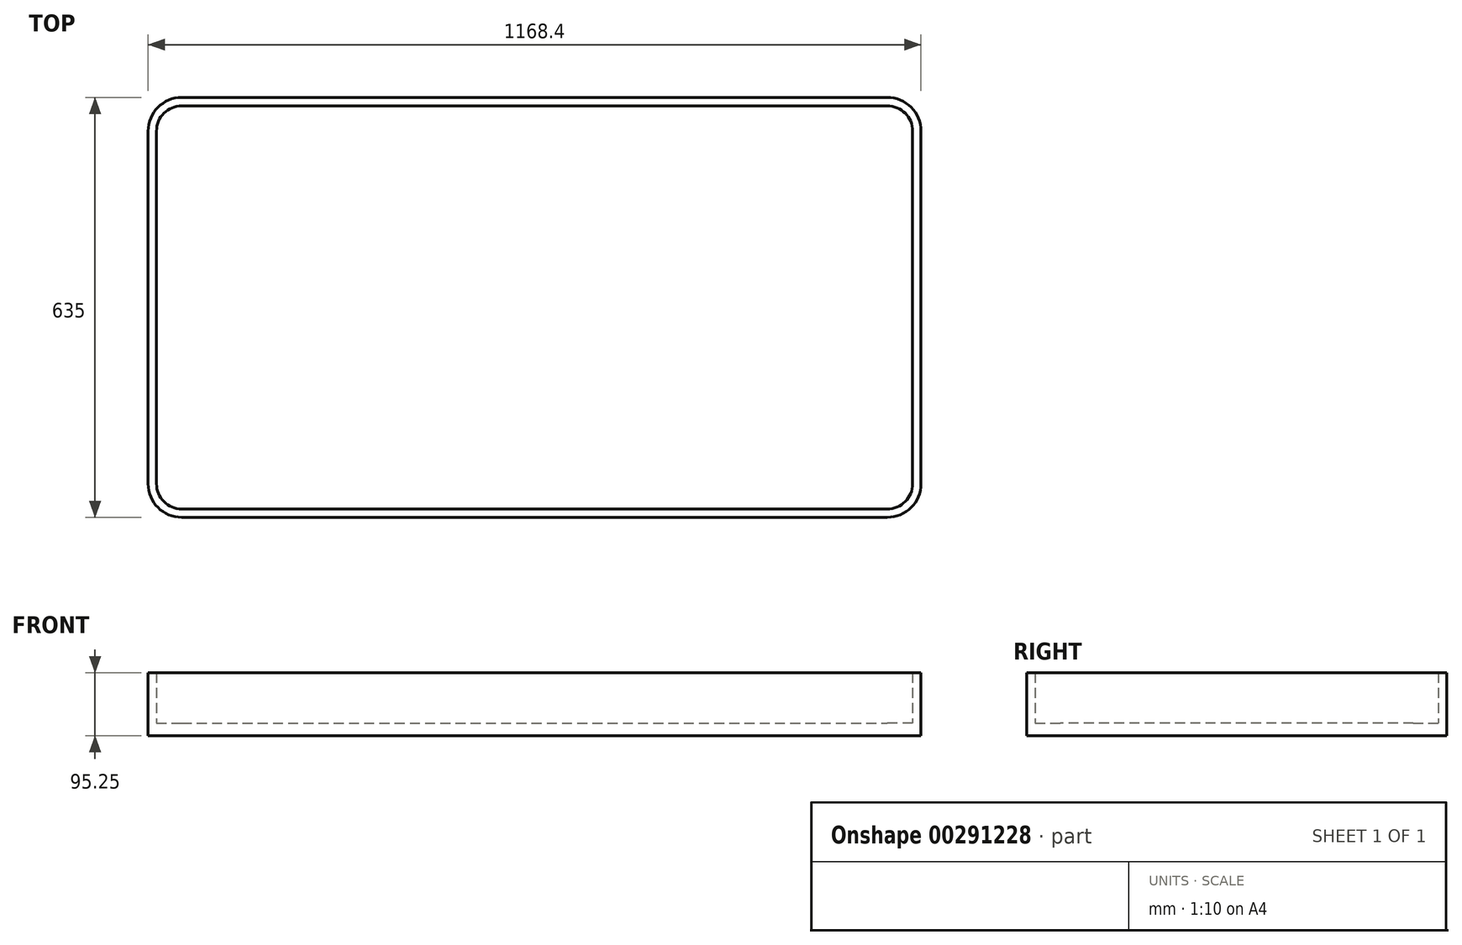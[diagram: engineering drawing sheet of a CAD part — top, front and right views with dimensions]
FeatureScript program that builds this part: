
annotation { "Feature Type Name" : "Feature", "Feature Type Description" : "" }
export const myFeature = defineFeature(function(context is Context, id is Id, definition is map)
    precondition{}
    {
        {
            var Q0;
            Q0=qCreatedBy(makeId("Top.planeOp"),FACE);
            var sketch = newSketch(context, id + "F0", { "sketchPlane" : qUnion([Q0])});
            skLineSegment(sketch, "E0.bottom", {"start": v(-533.4, 317.5) * mm, "end": v(533.4, 317.5) * mm});
            skLineSegment(sketch, "E0.top", {"start": v(-533.4, -317.5) * mm, "end": v(533.4, -317.5) * mm});
            skLineSegment(sketch, "E0.left", {"start": v(-584.2, 266.7) * mm, "end": v(-584.2, -266.7) * mm});
            skLineSegment(sketch, "E0.right", {"start": v(584.2, 266.7) * mm, "end": v(584.2, -266.7) * mm});
            skPoint(sketch, "E1.visualSharp", {"position": v(-584.2, 317.5) * mm});
            skArc(sketch, "E1.filletArc", {"start": v(-533.4, 317.5) * mm, "mid": v(-569.32, 302.62) * mm, "end": v(-584.2, 266.7) * mm});
            skPoint(sketch, "E2.visualSharp", {"position": v(584.2, 317.5) * mm});
            skArc(sketch, "E2.filletArc", {"start": v(584.2, 266.7) * mm, "mid": v(569.32, 302.62) * mm, "end": v(533.4, 317.5) * mm});
            skPoint(sketch, "E3.visualSharp", {"position": v(584.2, -317.5) * mm});
            skArc(sketch, "E3.filletArc", {"start": v(533.4, -317.5) * mm, "mid": v(569.32, -302.62) * mm, "end": v(584.2, -266.7) * mm});
            skPoint(sketch, "E4.visualSharp", {"position": v(-584.2, -317.5) * mm});
            skArc(sketch, "E4.filletArc", {"start": v(-584.2, -266.7) * mm, "mid": v(-569.32, -302.62) * mm, "end": v(-533.4, -317.5) * mm});
            skSolve(sketch);
        }
        {
            var Q0;
            Q0 = qSketchRegion(id + "F0", true);
            extrude(context, id + "F1", {"entities" : qUnion([Q0]), "depth" : 19.05 * mm});
        }
        {
            var Q0;
            Q0=makeQuery(id+"F1.opExtrude","CAP_FACE",FACE,{"disambiguationData":[OSD([sQuery(id+"F0.wireOp",EDGE,"E0.bottom"),sQuery(id+"F0.wireOp",EDGE,"E0.top"),sQuery(id+"F0.wireOp",EDGE,"E0.left"),sQuery(id+"F0.wireOp",EDGE,"E0.right"),sQuery(id+"F0.wireOp",EDGE,"E1.filletArc"),sQuery(id+"F0.wireOp",EDGE,"E2.filletArc"),sQuery(id+"F0.wireOp",EDGE,"E3.filletArc"),sQuery(id+"F0.wireOp",EDGE,"E4.filletArc")])],"isStart":false});
            var sketch = newSketch(context, id + "F2", { "sketchPlane" : qUnion([Q0])});
            skLineSegment(sketch, "E5.0", {"start": v(-571.5, 266.7) * mm, "end": v(-571.5, -266.7) * mm});
            skLineSegment(sketch, "E5.1", {"start": v(-533.4, 304.8) * mm, "end": v(533.4, 304.8) * mm});
            skLineSegment(sketch, "E5.2", {"start": v(571.5, 266.7) * mm, "end": v(571.5, -266.7) * mm});
            skLineSegment(sketch, "E5.3", {"start": v(-533.4, -304.8) * mm, "end": v(533.4, -304.8) * mm});
            skLineSegment(sketch, "E6.0", {"start": v(-590.55, 266.7) * mm, "end": v(-590.55, -266.7) * mm});
            skArc(sketch, "E6.1", {"start": v(-533.4, 323.85) * mm, "mid": v(-573.81, 307.11) * mm, "end": v(-590.55, 266.7) * mm});
            skArc(sketch, "E6.2", {"start": v(-590.55, -266.7) * mm, "mid": v(-573.81, -307.11) * mm, "end": v(-533.4, -323.85) * mm});
            skLineSegment(sketch, "E6.3", {"start": v(533.4, 323.85) * mm, "end": v(-533.4, 323.85) * mm});
            skLineSegment(sketch, "E6.4", {"start": v(-533.4, -323.85) * mm, "end": v(533.4, -323.85) * mm});
            skArc(sketch, "E6.5", {"start": v(533.4, -323.85) * mm, "mid": v(573.81, -307.11) * mm, "end": v(590.55, -266.7) * mm});
            skLineSegment(sketch, "E6.6", {"start": v(590.55, -266.7) * mm, "end": v(590.55, 266.7) * mm});
            skArc(sketch, "E6.7", {"start": v(590.55, 266.7) * mm, "mid": v(573.81, 307.11) * mm, "end": v(533.4, 323.85) * mm});
            skPoint(sketch, "E7.visualSharp", {"position": v(-571.5, 304.8) * mm});
            skArc(sketch, "E7.filletArc", {"start": v(-533.4, 304.8) * mm, "mid": v(-560.34, 293.64) * mm, "end": v(-571.5, 266.7) * mm});
            skPoint(sketch, "E8.visualSharp", {"position": v(571.5, 304.8) * mm});
            skArc(sketch, "E8.filletArc", {"start": v(571.5, 266.7) * mm, "mid": v(560.34, 293.64) * mm, "end": v(533.4, 304.8) * mm});
            skPoint(sketch, "E9.visualSharp", {"position": v(571.5, -304.8) * mm});
            skArc(sketch, "E9.filletArc", {"start": v(533.4, -304.8) * mm, "mid": v(560.34, -293.64) * mm, "end": v(571.5, -266.7) * mm});
            skPoint(sketch, "E10.visualSharp", {"position": v(-571.5, -304.8) * mm});
            skArc(sketch, "E10.filletArc", {"start": v(-571.5, -266.7) * mm, "mid": v(-560.34, -293.64) * mm, "end": v(-533.4, -304.8) * mm});
            skSolve(sketch);
        }
        {
            var Q0;
            Q0=makeQuery(id+"F2.imprint","IMPRINT",FACE,{"disambiguationData":[TD([[makeQuery(id+"F2.imprint","IMPRINT",EDGE,{"derivedFrom":sQuery(id+"F2.wireOp",EDGE,"xitZLcKN-yIl8-IpYT-J6Ye-wkeivL7j65dY.bottom")}),1.0]])]});
            var Q1;
            Q1=makeQuery(id+"F2.imprint","IMPRINT",FACE,{"disambiguationData":[TD([[makeQuery(id+"F2.imprint","IMPRINT",EDGE,{"derivedFrom":sQuery(id+"F2.wireOp",EDGE,"E5.0")}),-1.0]])]});
            extrude(context, id + "F3", {"entities" : qUnion([Q0, Q1]), "operationType" : NewBodyOperationType.ADD, "depth" : 76.2 * mm});
        }
    });
